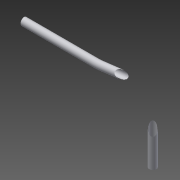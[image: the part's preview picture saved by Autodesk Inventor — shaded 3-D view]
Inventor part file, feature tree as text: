
AUTODESK INVENTOR PART (.ipt)
format: ipt  version: 2015 (Build 190159000, 159)  size: 189,440 bytes
history: native  units: mm
features: sketch x5, other x4, extrude x2, shell x1
ambient origin geometry x8: Origin, YZ Plane, XZ Plane, XY Plane, X Axis, Y Axis, Z Axis, Center Point
bodies: Body1 (feature_tree)
feature tree (12):
  other  "Bryła1"
  extrude  "Wyciągnięcie proste1"  Depth=32.0mm
  shell  "Skorupa1"  Thickness=815.0mm
  other  "Gięcie części1"
  sketch  "Szkic7"
  other  "Płaszczyzna konstrukcyjna4"
  other  "Gięcie części2"
  extrude  "Wyciągnięcie proste4"  Depth=2.0mm
  sketch  "Szkic1"
  sketch  "Szkic4"
  sketch  "Szkic8"
  sketch  "Szkic10"
